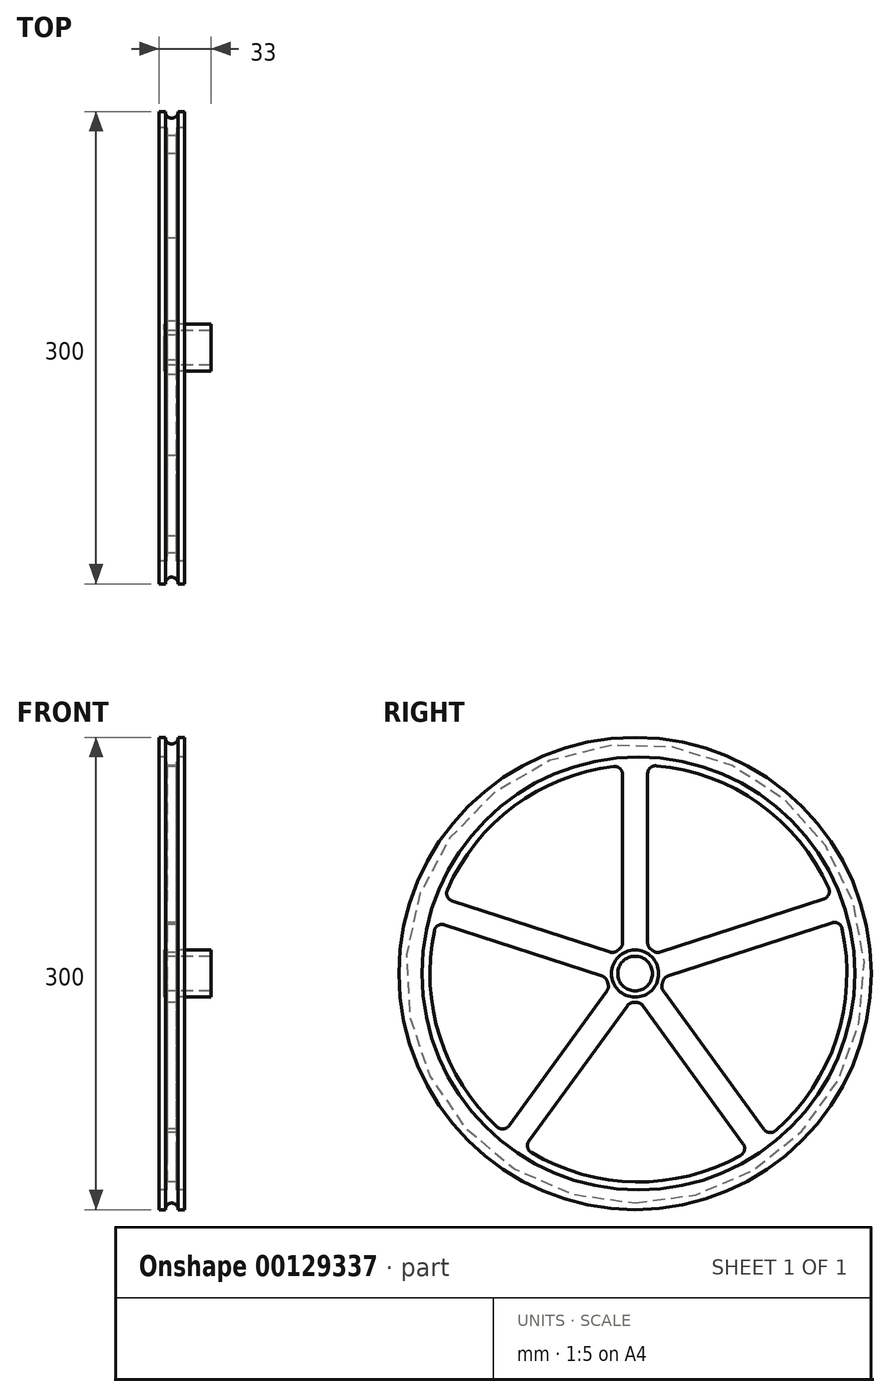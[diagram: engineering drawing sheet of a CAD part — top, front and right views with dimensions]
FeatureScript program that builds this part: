
annotation { "Feature Type Name" : "Feature", "Feature Type Description" : "" }
export const myFeature = defineFeature(function(context is Context, id is Id, definition is map)
    precondition{}
    {
        {
            var Q0;
            Q0=qCreatedBy(makeId("Right.planeOp"),FACE);
            var sketch = newSketch(context, id + "F0", { "sketchPlane" : qUnion([Q0])});
            skCircle(sketch, "E0", {"center": v(0, 0) * mm, "radius": 11 * mm});
            skCircle(sketch, "E1", {"center": v(0, 0) * mm, "radius": 15 * mm});
            skCircle(sketch, "E2", {"center": v(0, 0) * mm, "radius": 150 * mm});
            skCircle(sketch, "E3", {"center": v(2.11, 0) * mm, "radius": 137.5 * mm});
            skArc(sketch, "E4", {"start": v(122.97, 54.19) * mm, "mid": v(78.8, 108) * mm, "end": v(13.43, 131.97) * mm});
            skArc(sketch, "E5", {"start": v(-17.7, -5) * mm, "mid": v(-17.5, -5.68) * mm, "end": v(-17.26, -6.36) * mm});
            skPoint(sketch, "E6.orphan", {"position": v(140.02, 37.08) * mm});
            skArc(sketch, "E7.trimOffspring", {"start": v(89.15, -99.84) * mm, "mid": v(127.9, -41.45) * mm, "end": v(131.45, 28.53) * mm});
            skArc(sketch, "E8.trimOffspring", {"start": v(-65.94, -113.63) * mm, "mid": v(0.33, -132.44) * mm, "end": v(67.08, -115.42) * mm});
            skArc(sketch, "E9.trimOffspring", {"start": v(-127.52, 27.2) * mm, "mid": v(-124.03, -40.4) * mm, "end": v(-87.59, -97.45) * mm});
            skArc(sketch, "E10.trimOffspring", {"start": v(-13.6, 131.52) * mm, "mid": v(-76.9, 106.3) * mm, "end": v(-119.3, 52.94) * mm});
            skPoint(sketch, "E11.visualSharp", {"position": v(8, 132.32) * mm});
            skArc(sketch, "E11.filletArc", {"start": v(13.43, 131.97) * mm, "mid": v(9.62, 130.67) * mm, "end": v(8, 126.98) * mm});
            skPoint(sketch, "E12.visualSharp", {"position": v(-8, 132.06) * mm});
            skArc(sketch, "E12.filletArc", {"start": v(-8, 126.55) * mm, "mid": v(-9.68, 130.3) * mm, "end": v(-13.6, 131.52) * mm});
            skPoint(sketch, "E13.visualSharp", {"position": v(125.14, 49.07) * mm});
            skArc(sketch, "E13.filletArc", {"start": v(119.95, 47.39) * mm, "mid": v(122.98, 50.11) * mm, "end": v(122.97, 54.19) * mm});
            skPoint(sketch, "E14.visualSharp", {"position": v(130.16, 33.88) * mm});
            skArc(sketch, "E14.filletArc", {"start": v(131.45, 28.53) * mm, "mid": v(129.05, 31.8) * mm, "end": v(125.03, 32.21) * mm});
            skPoint(sketch, "E15.visualSharp", {"position": v(84.97, -103.34) * mm});
            skArc(sketch, "E15.filletArc", {"start": v(81.82, -99) * mm, "mid": v(85.3, -101.04) * mm, "end": v(89.15, -99.84) * mm});
            skPoint(sketch, "E16.visualSharp", {"position": v(71.9, -112.57) * mm});
            skArc(sketch, "E16.filletArc", {"start": v(67.08, -115.42) * mm, "mid": v(69.51, -112.13) * mm, "end": v(68.67, -108.13) * mm});
            skPoint(sketch, "E17.visualSharp", {"position": v(-70.56, -110.73) * mm});
            skArc(sketch, "E17.filletArc", {"start": v(-67.42, -106.4) * mm, "mid": v(-68.27, -110.34) * mm, "end": v(-65.94, -113.63) * mm});
            skPoint(sketch, "E18.visualSharp", {"position": v(-83.39, -101.16) * mm});
            skArc(sketch, "E18.filletArc", {"start": v(-87.59, -97.45) * mm, "mid": v(-83.7, -98.75) * mm, "end": v(-80.16, -96.71) * mm});
            skPoint(sketch, "E19.visualSharp", {"position": v(-126.26, 32.61) * mm});
            skArc(sketch, "E19.filletArc", {"start": v(-121.08, 30.93) * mm, "mid": v(-125.13, 30.5) * mm, "end": v(-127.52, 27.2) * mm});
            skPoint(sketch, "E20.visualSharp", {"position": v(-121.4, 47.85) * mm});
            skArc(sketch, "E20.filletArc", {"start": v(-119.3, 52.94) * mm, "mid": v(-119.27, 48.9) * mm, "end": v(-116.26, 46.19) * mm});
            skLineSegment(sketch, "E21.trimOffspring", {"start": v(20.97, -1.6) * mm, "end": v(125.03, 32.21) * mm});
            skLineSegment(sketch, "E22.trimOffspring", {"start": v(17.9, -11.03) * mm, "end": v(81.82, -99) * mm});
            skPoint(sketch, "E23.orphan", {"position": v(6.47, -4.7) * mm});
            skLineSegment(sketch, "E24.trimOffspring", {"start": v(16.02, 13.62) * mm, "end": v(119.95, 47.39) * mm});
            skLineSegment(sketch, "E25.trimOffspring", {"start": v(8, 19.45) * mm, "end": v(8, 126.98) * mm});
            skLineSegment(sketch, "E26.trimOffspring", {"start": v(-16.02, 13.62) * mm, "end": v(-116.26, 46.19) * mm});
            skLineSegment(sketch, "E27.trimOffspring", {"start": v(-8, 19.45) * mm, "end": v(-8, 126.55) * mm});
            skLineSegment(sketch, "E28.trimOffspring", {"start": v(-20.97, -1.6) * mm, "end": v(-121.08, 30.93) * mm});
            skLineSegment(sketch, "E29.trimOffspring", {"start": v(-17.9, -11.03) * mm, "end": v(-80.16, -96.71) * mm});
            skArc(sketch, "E30.trimOffspring", {"start": v(-10.22, 15.3) * mm, "mid": v(-10.81, 14.88) * mm, "end": v(-11.38, 14.45) * mm});
            skArc(sketch, "E31.trimOffspring", {"start": v(11.38, 14.45) * mm, "mid": v(10.81, 14.88) * mm, "end": v(10.22, 15.3) * mm});
            skLineSegment(sketch, "E32.trimOffspring", {"start": v(4.96, -20.44) * mm, "end": v(68.67, -108.13) * mm});
            skLineSegment(sketch, "E33.trimOffspring", {"start": v(-4.96, -20.44) * mm, "end": v(-67.42, -106.4) * mm});
            skArc(sketch, "E34.trimOffspring", {"start": v(-0.72, -18.38) * mm, "mid": v(0, -18.4) * mm, "end": v(0.72, -18.38) * mm});
            skArc(sketch, "E35.trimOffspring", {"start": v(17.26, -6.36) * mm, "mid": v(17.5, -5.68) * mm, "end": v(17.7, -5) * mm});
            skPoint(sketch, "E36.visualSharp", {"position": v(13.28, 12.73) * mm});
            skArc(sketch, "E36.filletArc", {"start": v(11.38, 14.45) * mm, "mid": v(13.6, 13.45) * mm, "end": v(16.02, 13.62) * mm});
            skPoint(sketch, "E37.visualSharp", {"position": v(8, 16.56) * mm});
            skArc(sketch, "E37.filletArc", {"start": v(8, 19.45) * mm, "mid": v(8.6, 17.1) * mm, "end": v(10.22, 15.3) * mm});
            skPoint(sketch, "E38.visualSharp", {"position": v(-8, 16.56) * mm});
            skArc(sketch, "E38.filletArc", {"start": v(-10.22, 15.3) * mm, "mid": v(-8.6, 17.1) * mm, "end": v(-8, 19.45) * mm});
            skPoint(sketch, "E39.visualSharp", {"position": v(-13.28, 12.73) * mm});
            skArc(sketch, "E39.filletArc", {"start": v(-16.02, 13.62) * mm, "mid": v(-13.6, 13.45) * mm, "end": v(-11.38, 14.45) * mm});
            skPoint(sketch, "E40.visualSharp", {"position": v(-18.22, -2.5) * mm});
            skArc(sketch, "E40.filletArc", {"start": v(-17.7, -5) * mm, "mid": v(-18.9, -2.89) * mm, "end": v(-20.97, -1.6) * mm});
            skPoint(sketch, "E41.visualSharp", {"position": v(-16.2, -8.7) * mm});
            skArc(sketch, "E41.filletArc", {"start": v(-17.9, -11.03) * mm, "mid": v(-17, -8.78) * mm, "end": v(-17.26, -6.36) * mm});
            skPoint(sketch, "E42.visualSharp", {"position": v(-3.26, -18.1) * mm});
            skArc(sketch, "E42.filletArc", {"start": v(-0.72, -18.38) * mm, "mid": v(-3.1, -18.88) * mm, "end": v(-4.96, -20.44) * mm});
            skPoint(sketch, "E43.visualSharp", {"position": v(3.26, -18.1) * mm});
            skArc(sketch, "E43.filletArc", {"start": v(4.96, -20.44) * mm, "mid": v(3.1, -18.88) * mm, "end": v(0.72, -18.38) * mm});
            skPoint(sketch, "E44.visualSharp", {"position": v(16.2, -8.7) * mm});
            skArc(sketch, "E44.filletArc", {"start": v(17.26, -6.36) * mm, "mid": v(17, -8.78) * mm, "end": v(17.9, -11.03) * mm});
            skPoint(sketch, "E45.visualSharp", {"position": v(18.22, -2.5) * mm});
            skArc(sketch, "E45.filletArc", {"start": v(20.97, -1.6) * mm, "mid": v(18.9, -2.89) * mm, "end": v(17.7, -5) * mm});
            skSolve(sketch);
        }
        {
            var Q0;
            Q0 = qSketchRegion(id + "F0", true);
            extrude(context, id + "F1", {"entities" : qUnion([Q0]), "depth" : 8 * mm, "hasSecondDirection" : true, "secondDirectionOppositeDirection" : true, "secondDirectionDepth" : 8 * mm});
        }
        {
            var Q0;
            Q0=makeQuery(id+"F0.imprint","IMPRINT",FACE,{"disambiguationData":[TD([[makeQuery(id+"F0.imprint","IMPRINT",EDGE,{"derivedFrom":sQuery(id+"F0.wireOp",EDGE,"E1")}),-1.0]])]});
            extrude(context, id + "F2", {"entities" : qUnion([Q0]), "operationType" : NewBodyOperationType.ADD, "depth" : 3 * mm, "hasSecondDirection" : true, "secondDirectionOppositeDirection" : true, "secondDirectionDepth" : 3 * mm});
        }
        {
            var Q0;
            Q0=makeQuery(id+"F0.imprint","IMPRINT",FACE,{"disambiguationData":[TD([[makeQuery(id+"F0.imprint","IMPRINT",EDGE,{"derivedFrom":sQuery(id+"F0.wireOp",EDGE,"E0")}),-1.0]])]});
            extrude(context, id + "F3", {"entities" : qUnion([Q0]), "operationType" : NewBodyOperationType.ADD, "depth" : 25 * mm, "hasSecondDirection" : true, "secondDirectionOppositeDirection" : true, "secondDirectionDepth" : 5 * mm});
        }
        {
            var Q0;
            Q0=qCreatedBy(makeId("Front.planeOp"),FACE);
            var sketch = newSketch(context, id + "F4", { "sketchPlane" : qUnion([Q0])});
            skCircle(sketch, "E46", {"center": v(0, -149.75) * mm, "radius": 4 * mm});
            skSolve(sketch);
        }
        {
            var Q0;
            Q0=makeQuery(id+"F4.imprint","IMPRINT",FACE,{"disambiguationData":[TD([[makeQuery(id+"F4.imprint","IMPRINT",EDGE,{"derivedFrom":sQuery(id+"F4.wireOp",EDGE,"E46")}),1.0]])]});
            var Q1;
            Q1=sQuery(id+"F0.wireOp",EDGE,"E2");
            revolve(context, id + "F5", {"operationType" : NewBodyOperationType.REMOVE, "entities" : qUnion([Q0]), "axis" : qUnion([Q1]), "revolveType" : RevolveType.FULL, "oppositeDirection" : true});
        }
    });
